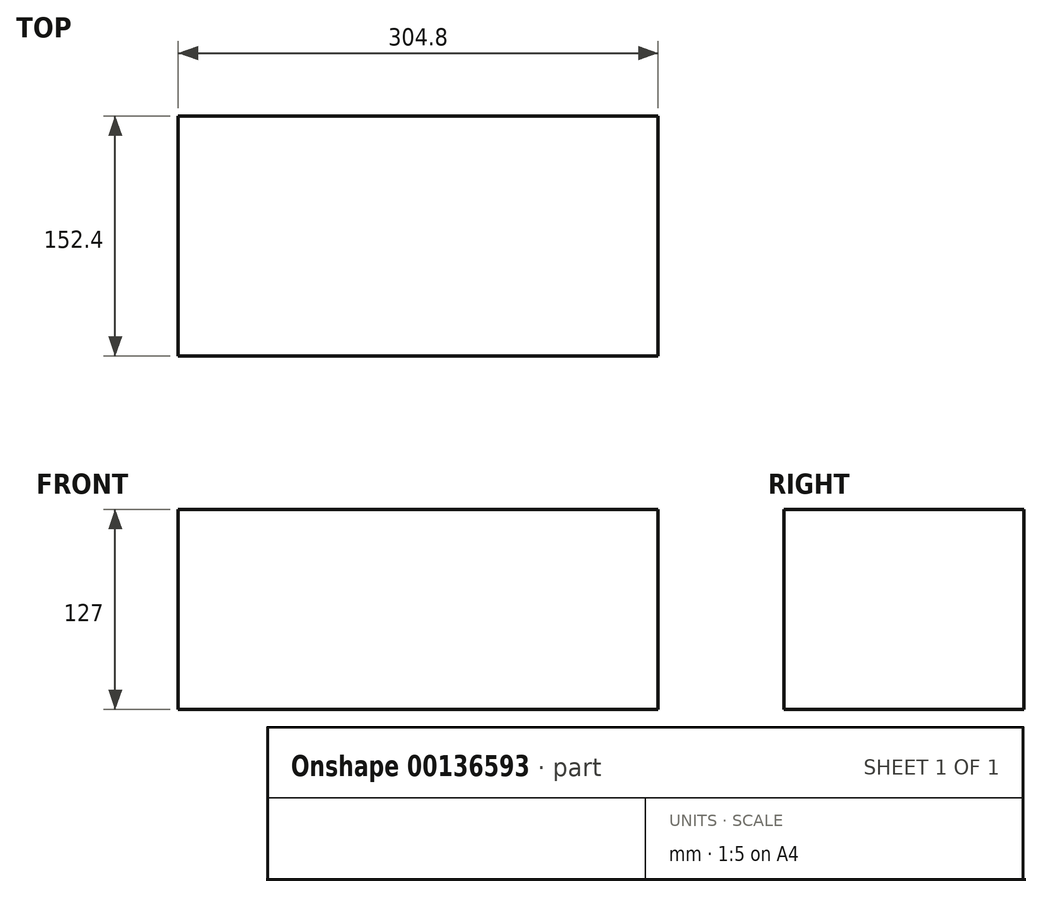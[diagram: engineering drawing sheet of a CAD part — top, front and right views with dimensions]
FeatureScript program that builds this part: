
annotation { "Feature Type Name" : "Feature", "Feature Type Description" : "" }
export const myFeature = defineFeature(function(context is Context, id is Id, definition is map)
    precondition{}
    {
        {
            var Q0;
            Q0=qCreatedBy(makeId("Top.planeOp"),FACE);
            var sketch = newSketch(context, id + "F0", { "sketchPlane" : qUnion([Q0])});
            skLineSegment(sketch, "E0.bottom", {"start": v(-154.22, 99.5) * mm, "end": v(150.58, 99.5) * mm});
            skLineSegment(sketch, "E0.top", {"start": v(-154.22, -52.9) * mm, "end": v(150.58, -52.9) * mm});
            skLineSegment(sketch, "E0.left", {"start": v(-154.22, 99.5) * mm, "end": v(-154.22, -52.9) * mm});
            skLineSegment(sketch, "E0.right", {"start": v(150.58, 99.5) * mm, "end": v(150.58, -52.9) * mm});
            skSolve(sketch);
        }
        {
            var Q0;
            Q0 = qSketchRegion(id + "F0", true);
            extrude(context, id + "F1", {"entities" : qUnion([Q0]), "depth" : 127 * mm});
        }
    });
